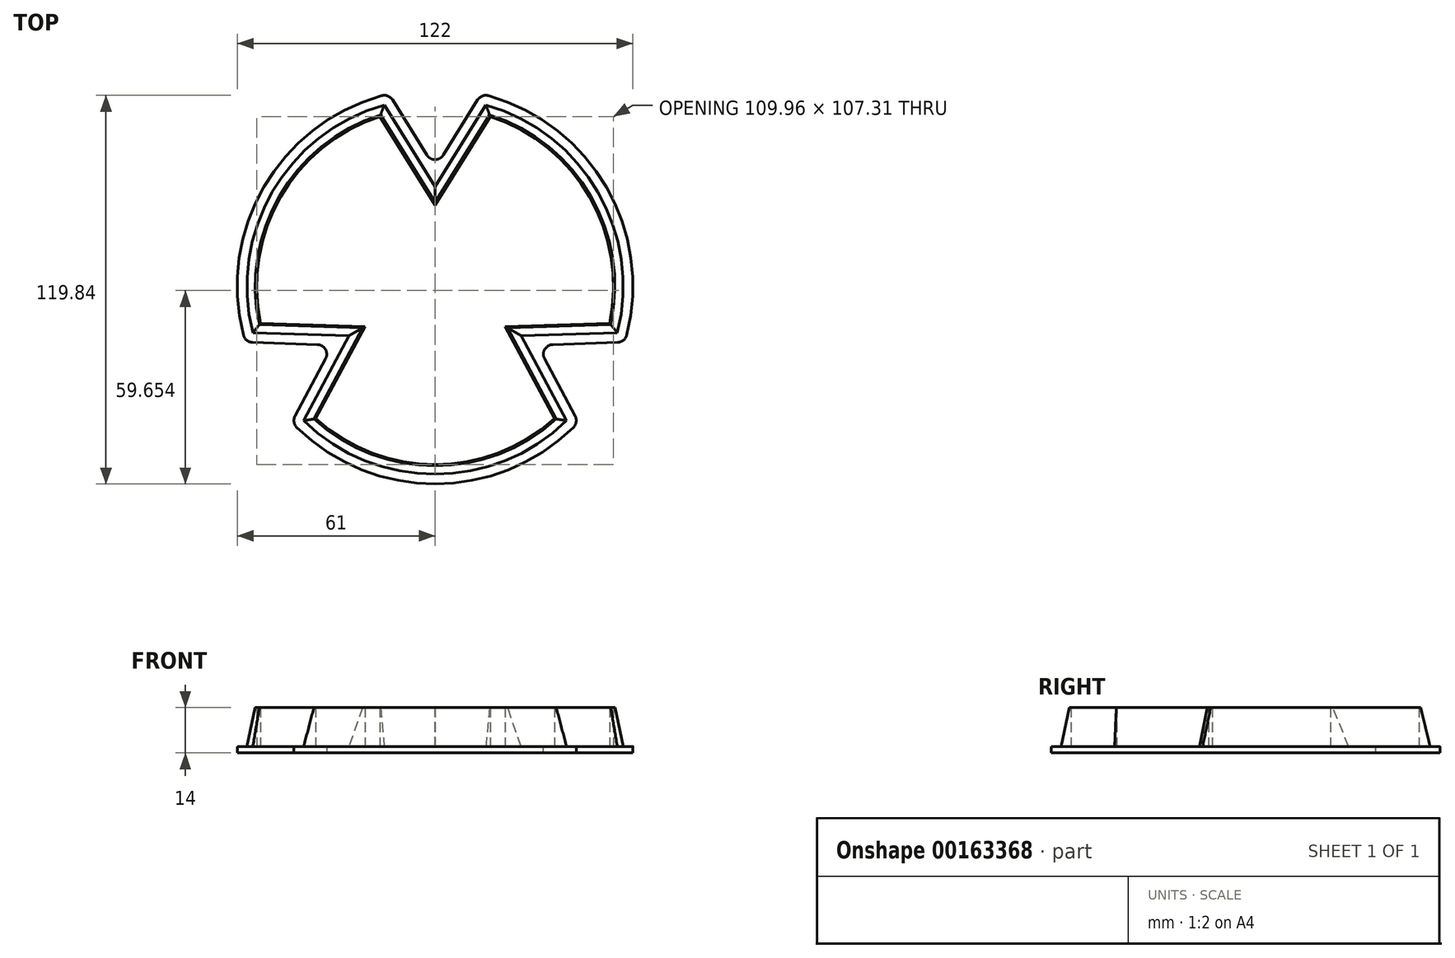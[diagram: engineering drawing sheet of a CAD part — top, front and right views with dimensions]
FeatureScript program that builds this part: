
annotation { "Feature Type Name" : "Feature", "Feature Type Description" : "" }
export const myFeature = defineFeature(function(context is Context, id is Id, definition is map)
    precondition{}
    {
        {
            var Q0;
            Q0=qCreatedBy(makeId("Top.planeOp"),FACE);
            var sketch = newSketch(context, id + "F0", { "sketchPlane" : qUnion([Q0])});
            skCircle(sketch, "E0", {"center": v(0, 0) * mm, "radius": 22 * mm, "construction": true});
            skArc(sketch, "E1", {"start": v(-17, 52.3) * mm, "mid": v(-47.63, 27.5) * mm, "end": v(-53.8, -11.44) * mm});
            skCircle(sketch, "E2", {"center": v(0, 0) * mm, "radius": 34 * mm, "construction": true});
            skCircle(sketch, "E3", {"center": v(0, 0) * mm, "radius": 25 * mm, "construction": true});
            skLineSegment(sketch, "E4", {"start": v(0, 0) * mm, "end": v(17, 52.3) * mm, "construction": true});
            skLineSegment(sketch, "E5", {"start": v(0, 0) * mm, "end": v(-17, 52.3) * mm, "construction": true});
            skLineSegment(sketch, "E6", {"start": v(0, 25) * mm, "end": v(17, 52.3) * mm});
            skLineSegment(sketch, "E7", {"start": v(0, 25) * mm, "end": v(-17, 52.3) * mm});
            skLineSegment(sketch, "E8", {"start": v(0, 0) * mm, "end": v(-47.63, -27.5) * mm, "construction": true});
            skLineSegment(sketch, "E9", {"start": v(0, 0) * mm, "end": v(47.63, -27.5) * mm, "construction": true});
            skLineSegment(sketch, "E10", {"start": v(0, 0) * mm, "end": v(0, 55) * mm, "construction": true});
            skLineSegment(sketch, "E11", {"start": v(0, 0) * mm, "end": v(-36.8, -40.87) * mm, "construction": true});
            skLineSegment(sketch, "E12", {"start": v(0, 0) * mm, "end": v(-53.8, -11.44) * mm, "construction": true});
            skLineSegment(sketch, "E13", {"start": v(0, 0) * mm, "end": v(36.8, -40.87) * mm, "construction": true});
            skLineSegment(sketch, "E14", {"start": v(53.8, -11.44) * mm, "end": v(0, 0) * mm, "construction": true});
            skLineSegment(sketch, "E15", {"start": v(-21.65, -12.5) * mm, "end": v(-36.8, -40.87) * mm});
            skLineSegment(sketch, "E16", {"start": v(-21.65, -12.5) * mm, "end": v(-53.8, -11.44) * mm});
            skLineSegment(sketch, "E17", {"start": v(21.65, -12.5) * mm, "end": v(36.8, -40.87) * mm});
            skLineSegment(sketch, "E18", {"start": v(21.65, -12.5) * mm, "end": v(53.8, -11.44) * mm});
            skArc(sketch, "E19.trimOffspring", {"start": v(53.8, -11.44) * mm, "mid": v(47.63, 27.5) * mm, "end": v(17, 52.3) * mm});
            skArc(sketch, "E20.trimOffspring", {"start": v(-36.8, -40.87) * mm, "mid": v(0, -55) * mm, "end": v(36.8, -40.87) * mm});
            skLineSegment(sketch, "E21.0", {"start": v(0, 30.68) * mm, "end": v(-15.66, 55.84) * mm});
            skLineSegment(sketch, "E21.1", {"start": v(0, 30.68) * mm, "end": v(15.66, 55.84) * mm});
            skArc(sketch, "E21.2", {"start": v(-15.66, 55.84) * mm, "mid": v(-50.23, 29) * mm, "end": v(-56.2, -14.36) * mm});
            skArc(sketch, "E21.3", {"start": v(56.2, -14.36) * mm, "mid": v(50.23, 29) * mm, "end": v(15.66, 55.84) * mm});
            skLineSegment(sketch, "E21.4", {"start": v(26.57, -15.34) * mm, "end": v(56.2, -14.36) * mm});
            skLineSegment(sketch, "E21.5", {"start": v(-26.57, -15.34) * mm, "end": v(-56.2, -14.36) * mm});
            skLineSegment(sketch, "E21.6", {"start": v(-26.57, -15.34) * mm, "end": v(-40.53, -41.49) * mm});
            skArc(sketch, "E21.7", {"start": v(-40.53, -41.49) * mm, "mid": v(0, -58) * mm, "end": v(40.53, -41.49) * mm});
            skLineSegment(sketch, "E21.8", {"start": v(26.57, -15.34) * mm, "end": v(40.53, -41.49) * mm});
            skSolve(sketch);
        }
        {
            var Q0;
            Q0 = qSketchRegion(id + "F0", true);
            extrude(context, id + "F1", {"entities" : qUnion([Q0]), "depth" : 12 * mm});
        }
        {
            var Q0;
            Q0=makeQuery(id+"F1.opExtrude","CAP_FACE",FACE,{"disambiguationData":[OSD([sQuery(id+"F0.wireOp",EDGE,"E1"),sQuery(id+"F0.wireOp",EDGE,"E6"),sQuery(id+"F0.wireOp",EDGE,"E7"),sQuery(id+"F0.wireOp",EDGE,"E15"),sQuery(id+"F0.wireOp",EDGE,"E16"),sQuery(id+"F0.wireOp",EDGE,"E17"),sQuery(id+"F0.wireOp",EDGE,"E18"),sQuery(id+"F0.wireOp",EDGE,"E19.trimOffspring"),sQuery(id+"F0.wireOp",EDGE,"E20.trimOffspring"),sQuery(id+"F0.wireOp",EDGE,"E21.0"),sQuery(id+"F0.wireOp",EDGE,"E21.1"),sQuery(id+"F0.wireOp",EDGE,"E21.2"),sQuery(id+"F0.wireOp",EDGE,"E21.3"),sQuery(id+"F0.wireOp",EDGE,"E21.4"),sQuery(id+"F0.wireOp",EDGE,"E21.5"),sQuery(id+"F0.wireOp",EDGE,"E21.6"),sQuery(id+"F0.wireOp",EDGE,"E21.7"),sQuery(id+"F0.wireOp",EDGE,"E21.8")])],"isStart":true});
            var sketch = newSketch(context, id + "F2", { "sketchPlane" : qUnion([Q0])});
            skLineSegment(sketch, "E22", {"start": v(-36.8, 40.87) * mm, "end": v(-21.65, 12.5) * mm});
            skLineSegment(sketch, "E23", {"start": v(-21.65, 12.5) * mm, "end": v(-53.8, 11.44) * mm});
            skArc(sketch, "E24", {"start": v(-53.8, 11.44) * mm, "mid": v(-47.63, -27.5) * mm, "end": v(-17, -52.3) * mm});
            skLineSegment(sketch, "E25", {"start": v(21.65, 12.5) * mm, "end": v(36.8, 40.87) * mm});
            skLineSegment(sketch, "E26", {"start": v(21.65, 12.5) * mm, "end": v(53.8, 11.44) * mm});
            skLineSegment(sketch, "E27", {"start": v(0, -25) * mm, "end": v(17, -52.3) * mm});
            skLineSegment(sketch, "E28", {"start": v(0, -25) * mm, "end": v(-17, -52.3) * mm});
            skArc(sketch, "E29.trimOffspring", {"start": v(36.8, 40.87) * mm, "mid": v(0, 55) * mm, "end": v(-36.8, 40.87) * mm});
            skArc(sketch, "E30.trimOffspring", {"start": v(17, -52.3) * mm, "mid": v(47.63, -27.5) * mm, "end": v(53.8, 11.44) * mm});
            skArc(sketch, "E31.0", {"start": v(44.22, 42.02) * mm, "mid": v(0, 61) * mm, "end": v(-44.22, 42.02) * mm});
            skLineSegment(sketch, "E31.1", {"start": v(31.48, 18.18) * mm, "end": v(44.22, 42.02) * mm});
            skLineSegment(sketch, "E31.2", {"start": v(-44.22, 42.02) * mm, "end": v(-31.48, 18.18) * mm});
            skLineSegment(sketch, "E31.3", {"start": v(31.48, 18.18) * mm, "end": v(58.5, 17.28) * mm});
            skArc(sketch, "E31.4", {"start": v(14.28, -59.3) * mm, "mid": v(52.83, -30.5) * mm, "end": v(58.5, 17.28) * mm});
            skLineSegment(sketch, "E31.5", {"start": v(-31.48, 18.18) * mm, "end": v(-58.5, 17.28) * mm});
            skArc(sketch, "E31.6", {"start": v(-58.5, 17.28) * mm, "mid": v(-52.83, -30.5) * mm, "end": v(-14.28, -59.3) * mm});
            skLineSegment(sketch, "E31.7", {"start": v(0, -36.36) * mm, "end": v(-14.28, -59.3) * mm});
            skLineSegment(sketch, "E31.8", {"start": v(0, -36.36) * mm, "end": v(14.28, -59.3) * mm});
            skSolve(sketch);
        }
        {
            var Q0;
            Q0 = qSketchRegion(id + "F2", true);
            extrude(context, id + "F3", {"entities" : qUnion([Q0]), "operationType" : NewBodyOperationType.ADD, "depth" : 2 * mm});
        }
        {
            var Q0;
            Q0=makeQuery(id+"F1.opExtrude","CAP_EDGE",EDGE,{"disambiguationData":[OSD([sQuery(id+"F0.wireOp",EDGE,"E21.5")])],"isStart":false});
            var Q1;
            Q1=makeQuery(id+"F1.opExtrude","CAP_EDGE",EDGE,{"disambiguationData":[OSD([sQuery(id+"F0.wireOp",EDGE,"E21.6")])],"isStart":false});
            var Q2;
            Q2=makeQuery(id+"F1.opExtrude","CAP_EDGE",EDGE,{"disambiguationData":[OSD([sQuery(id+"F0.wireOp",EDGE,"E21.7")])],"isStart":false});
            var Q3;
            Q3=makeQuery(id+"F1.opExtrude","CAP_EDGE",EDGE,{"disambiguationData":[OSD([sQuery(id+"F0.wireOp",EDGE,"E21.2")])],"isStart":false});
            var Q4;
            Q4=makeQuery(id+"F1.opExtrude","CAP_EDGE",EDGE,{"disambiguationData":[OSD([sQuery(id+"F0.wireOp",EDGE,"E21.0")])],"isStart":false});
            var Q5;
            Q5=makeQuery(id+"F1.opExtrude","CAP_EDGE",EDGE,{"disambiguationData":[OSD([sQuery(id+"F0.wireOp",EDGE,"E21.1")])],"isStart":false});
            var Q6;
            Q6=makeQuery(id+"F1.opExtrude","CAP_EDGE",EDGE,{"disambiguationData":[OSD([sQuery(id+"F0.wireOp",EDGE,"E21.3")])],"isStart":false});
            var Q7;
            Q7=makeQuery(id+"F1.opExtrude","CAP_EDGE",EDGE,{"disambiguationData":[OSD([sQuery(id+"F0.wireOp",EDGE,"E21.4")])],"isStart":false});
            var Q8;
            Q8=makeQuery(id+"F1.opExtrude","CAP_EDGE",EDGE,{"disambiguationData":[OSD([sQuery(id+"F0.wireOp",EDGE,"E21.8")])],"isStart":false});
            chamfer(context, id + "F4", {"entities" : qUnion([Q0, Q1, Q2, Q3, Q4, Q5, Q6, Q7, Q8]), "chamferType" : ChamferType.OFFSET_ANGLE, "width" : 12 * mm, "oppositeDirection" : false, "angle" : 12 * degree, "tangentPropagation" : true});
        }
        {
            var Q0;
            Q0=makeQuery(id+"F3.opExtrude","SWEPT_EDGE",EDGE,{"disambiguationData":[OSD([sQuery(id+"F2.wireOp",EDGE,"E31.5"),sQuery(id+"F2.wireOp",EDGE,"E31.6")])]});
            var Q1;
            Q1=makeQuery(id+"F3.opExtrude","SWEPT_EDGE",EDGE,{"disambiguationData":[OSD([sQuery(id+"F2.wireOp",EDGE,"E31.2"),sQuery(id+"F2.wireOp",EDGE,"E31.5")])]});
            var Q2;
            Q2=makeQuery(id+"F3.opExtrude","SWEPT_EDGE",EDGE,{"disambiguationData":[OSD([sQuery(id+"F2.wireOp",EDGE,"E31.0"),sQuery(id+"F2.wireOp",EDGE,"E31.2")])]});
            var Q3;
            Q3=makeQuery(id+"F3.opExtrude","SWEPT_EDGE",EDGE,{"disambiguationData":[OSD([sQuery(id+"F2.wireOp",EDGE,"E31.0"),sQuery(id+"F2.wireOp",EDGE,"E31.1")])]});
            var Q4;
            Q4=makeQuery(id+"F3.opExtrude","SWEPT_EDGE",EDGE,{"disambiguationData":[OSD([sQuery(id+"F2.wireOp",EDGE,"E31.1"),sQuery(id+"F2.wireOp",EDGE,"E31.3")])]});
            var Q5;
            Q5=makeQuery(id+"F3.opExtrude","SWEPT_EDGE",EDGE,{"disambiguationData":[OSD([sQuery(id+"F2.wireOp",EDGE,"E31.3"),sQuery(id+"F2.wireOp",EDGE,"E31.4")])]});
            var Q6;
            Q6=makeQuery(id+"F3.opExtrude","SWEPT_EDGE",EDGE,{"disambiguationData":[OSD([sQuery(id+"F2.wireOp",EDGE,"E31.4"),sQuery(id+"F2.wireOp",EDGE,"E31.8")])]});
            var Q7;
            Q7=makeQuery(id+"F3.opExtrude","SWEPT_EDGE",EDGE,{"disambiguationData":[OSD([sQuery(id+"F2.wireOp",EDGE,"E31.7"),sQuery(id+"F2.wireOp",EDGE,"E31.8")])]});
            var Q8;
            Q8=makeQuery(id+"F3.opExtrude","SWEPT_EDGE",EDGE,{"disambiguationData":[OSD([sQuery(id+"F2.wireOp",EDGE,"E31.6"),sQuery(id+"F2.wireOp",EDGE,"E31.7")])]});
            fillet(context, id + "F5", {"entities" : qUnion([Q0, Q1, Q2, Q3, Q4, Q5, Q6, Q7, Q8]), "radius" : 3 * mm, "tangentPropagation" : true, "allowEdgeOverflow" : false});
        }
    });
